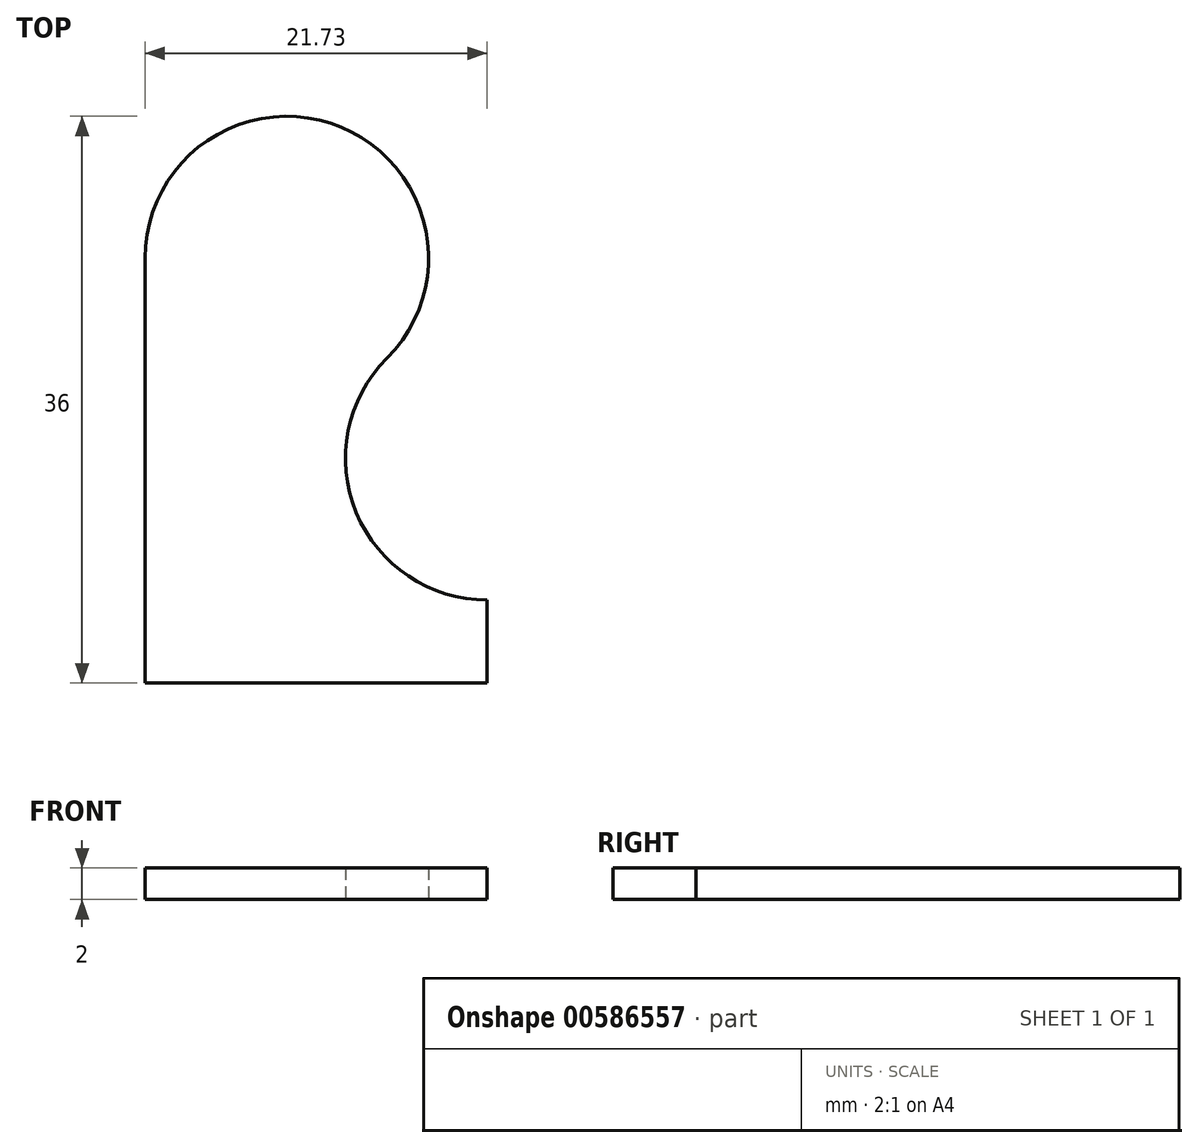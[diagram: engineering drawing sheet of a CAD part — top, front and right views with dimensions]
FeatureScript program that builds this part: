
annotation { "Feature Type Name" : "Feature", "Feature Type Description" : "" }
export const myFeature = defineFeature(function(context is Context, id is Id, definition is map)
    precondition{}
    {
        {
            var Q0;
            Q0=qCreatedBy(makeId("Top.planeOp"),FACE);
            var sketch = newSketch(context, id + "F0", { "sketchPlane" : qUnion([Q0])});
            skLineSegment(sketch, "E0", {"start": v(0, 0) * mm, "end": v(0, 27) * mm});
            skArc(sketch, "E1", {"start": v(0, 27) * mm, "mid": v(12.44, 35.31) * mm, "end": v(15.36, 20.64) * mm});
            skArc(sketch, "E2", {"start": v(15.36, 20.64) * mm, "mid": v(13.41, 10.83) * mm, "end": v(21.73, 5.27) * mm});
            skLineSegment(sketch, "E3", {"start": v(9, 27) * mm, "end": v(21.73, 14.27) * mm, "construction": true});
            skLineSegment(sketch, "E4", {"start": v(21.73, 0) * mm, "end": v(21.73, 14.27) * mm, "construction": true});
            skLineSegment(sketch, "E5", {"start": v(0, 0) * mm, "end": v(21.73, 0) * mm});
            skLineSegment(sketch, "E6", {"start": v(21.73, 5.27) * mm, "end": v(21.73, 0) * mm});
            skLineSegment(sketch, "E7", {"start": v(0, 27) * mm, "end": v(9, 27) * mm, "construction": true});
            skLineSegment(sketch, "E8", {"start": v(9, 27) * mm, "end": v(9, 18) * mm, "construction": true});
            skLineSegment(sketch, "E9", {"start": v(9, 18) * mm, "end": v(9, 9) * mm, "construction": true});
            skLineSegment(sketch, "E10", {"start": v(9, 0) * mm, "end": v(9, 9) * mm, "construction": true});
            skSolve(sketch);
        }
        {
            var Q0;
            Q0=qSketchRegion(id+"F0",true);
            extrude(context, id + "F1", {"entities" : qUnion([Q0]), "depth" : 2 * mm, "offsetDistance" : 25 * mm});
        }
    });
